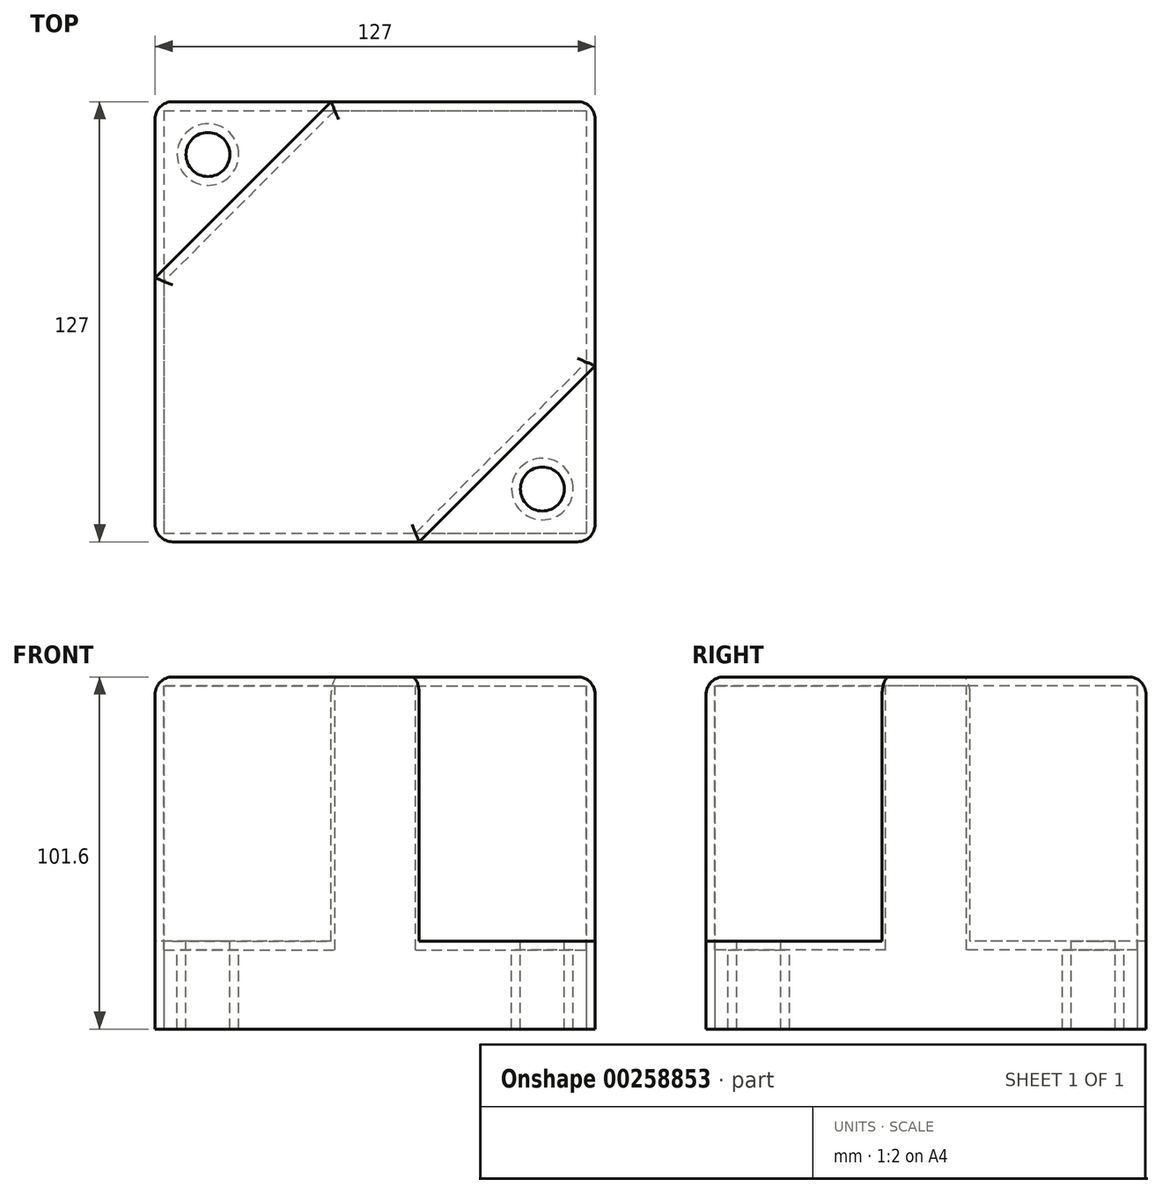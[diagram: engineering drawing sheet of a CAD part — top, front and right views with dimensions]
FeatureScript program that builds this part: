
annotation { "Feature Type Name" : "Feature", "Feature Type Description" : "" }
export const myFeature = defineFeature(function(context is Context, id is Id, definition is map)
    precondition{}
    {
        {
            var Q0;
            Q0=qCreatedBy(makeId("Top.planeOp"),FACE);
            var sketch = newSketch(context, id + "F0", { "sketchPlane" : qUnion([Q0])});
            skLineSegment(sketch, "E0.bottom", {"start": v(-61.5, 64.93) * mm, "end": v(65.5, 64.93) * mm});
            skLineSegment(sketch, "E0.top", {"start": v(-61.5, -62.07) * mm, "end": v(65.5, -62.07) * mm});
            skLineSegment(sketch, "E0.left", {"start": v(-61.5, 64.93) * mm, "end": v(-61.5, -62.07) * mm});
            skLineSegment(sketch, "E0.right", {"start": v(65.5, 64.93) * mm, "end": v(65.5, -62.07) * mm});
            skSolve(sketch);
        }
        {
            var Q0;
            Q0 = qSketchRegion(id + "F0", true);
            var Q1;
            Q1 = qSketchRegion(id + "F2", true);
            extrude(context, id + "F1", {"entities" : qUnion([Q0, Q1]), "depth" : 101.6 * mm});
        }
        {
            var Q0;
            Q0=makeQuery(id+"F1.opExtrude","CAP_FACE",FACE,{"disambiguationData":[OSD([sQuery(id+"F0.wireOp",EDGE,"E0.bottom"),sQuery(id+"F0.wireOp",EDGE,"E0.top"),sQuery(id+"F0.wireOp",EDGE,"E0.left"),sQuery(id+"F0.wireOp",EDGE,"E0.right")])],"isStart":false});
            var sketch = newSketch(context, id + "F2", { "sketchPlane" : qUnion([Q0])});
            skLineSegment(sketch, "E1", {"start": v(-10.7, 64.93) * mm, "end": v(-61.5, 14.13) * mm});
            skLineSegment(sketch, "E2", {"start": v(-10.7, 64.93) * mm, "end": v(-61.5, 64.93) * mm});
            skLineSegment(sketch, "E3", {"start": v(-61.5, 64.93) * mm, "end": v(-61.5, 14.13) * mm});
            skLineSegment(sketch, "E4", {"start": v(14.7, -62.07) * mm, "end": v(65.5, -11.27) * mm});
            skLineSegment(sketch, "E5", {"start": v(65.5, -11.27) * mm, "end": v(65.5, -62.07) * mm});
            skLineSegment(sketch, "E6", {"start": v(65.5, -62.07) * mm, "end": v(14.7, -62.07) * mm});
            skSolve(sketch);
        }
        {
            var Q0;
            Q0=makeQuery(id+"F2.imprint","IMPRINT",FACE,{"disambiguationData":[TD([[makeQuery(id+"F2.imprint","IMPRINT",EDGE,{"derivedFrom":sQuery(id+"F2.wireOp",EDGE,"E1")}),-1.0]])]});
            var Q1;
            Q1=makeQuery(id+"F2.imprint","IMPRINT",FACE,{"disambiguationData":[TD([[makeQuery(id+"F2.imprint","IMPRINT",EDGE,{"derivedFrom":sQuery(id+"F2.wireOp",EDGE,"E4")}),-1.0]])]});
            extrude(context, id + "F3", {"entities" : qUnion([Q0, Q1]), "operationType" : NewBodyOperationType.REMOVE, "oppositeDirection" : true, "depth" : 76.2 * mm});
        }
        {
            var Q0;
            Q0=makeQuery(id+"F3.boolean.opBoolean","COPY",FACE,{"derivedFrom":makeQuery(id+"F3.opExtrude","CAP_FACE",FACE,{"disambiguationData":[OSD([sQuery(id+"F2.wireOp",EDGE,"E1"),sQuery(id+"F2.wireOp",EDGE,"E2"),sQuery(id+"F2.wireOp",EDGE,"E3")])],"isStart":false})});
            var sketch = newSketch(context, id + "F4", { "sketchPlane" : qUnion([Q0])});
            skCircle(sketch, "E7", {"center": v(-46.26, 49.69) * mm, "radius": 6.35 * mm});
            skCircle(sketch, "E8", {"center": v(50.26, -46.83) * mm, "radius": 6.35 * mm});
            skSolve(sketch);
        }
        {
            var Q0;
            Q0 = qSketchRegion(id + "F4", true);
            extrude(context, id + "F5", {"entities" : qUnion([Q0]), "operationType" : NewBodyOperationType.REMOVE, "oppositeDirection" : true, "depth" : 203.2 * mm});
        }
        {
            var Q0;
            Q0=makeQuery(id+"F1.opExtrude","CAP_FACE",FACE,{"disambiguationData":[OSD([sQuery(id+"F0.wireOp",EDGE,"E0.bottom"),sQuery(id+"F0.wireOp",EDGE,"E0.top"),sQuery(id+"F0.wireOp",EDGE,"E0.left"),sQuery(id+"F0.wireOp",EDGE,"E0.right")])],"isStart":true});
            shell(context, id + "F6", {"entities" : qUnion([Q0]), "thickness" : 2.54 * mm});
        }
        {
            var Q0;
            Q0=makeQuery(id+"F3.boolean.opBoolean","COPY",EDGE,{"derivedFrom":makeQuery(id+"F3.opExtrude","CAP_EDGE",EDGE,{"disambiguationData":[OSD([sQuery(id+"F2.wireOp",EDGE,"E1")])],"isStart":true})});
            var Q1;
            Q1=makeQuery(id+"F1.opExtrude","CAP_EDGE",EDGE,{"disambiguationData":[OSD([sQuery(id+"F0.wireOp",EDGE,"E0.left")])],"isStart":false});
            var Q2;
            Q2=makeQuery(id+"F1.opExtrude","CAP_EDGE",EDGE,{"disambiguationData":[OSD([sQuery(id+"F0.wireOp",EDGE,"E0.top")])],"isStart":false});
            var Q3;
            Q3=makeQuery(id+"F1.opExtrude","CAP_FACE",FACE,{"disambiguationData":[OSD([sQuery(id+"F0.wireOp",EDGE,"E0.bottom"),sQuery(id+"F0.wireOp",EDGE,"E0.top"),sQuery(id+"F0.wireOp",EDGE,"E0.left"),sQuery(id+"F0.wireOp",EDGE,"E0.right")])],"isStart":false});
            var Q4;
            Q4=makeQuery(id+"F3.boolean.opBoolean","COPY",EDGE,{"derivedFrom":makeQuery(id+"F3.opExtrude","SWEPT_EDGE",EDGE,{"disambiguationData":[OSD([sQuery(id+"F0.wireOp",EDGE,"E0.left"),sQuery(id+"F2.wireOp",EDGE,"E1"),sQuery(id+"F2.wireOp",EDGE,"E3")])]})});
            var Q5;
            Q5=makeQuery(id+"F3.boolean.opBoolean","COPY",EDGE,{"derivedFrom":makeQuery(id+"F3.opExtrude","SWEPT_EDGE",EDGE,{"disambiguationData":[OSD([sQuery(id+"F0.wireOp",EDGE,"E0.bottom"),sQuery(id+"F2.wireOp",EDGE,"E1"),sQuery(id+"F2.wireOp",EDGE,"E2")])]})});
            var Q6;
            Q6=makeQuery(id+"F3.boolean.opBoolean","COPY",EDGE,{"derivedFrom":makeQuery(id+"F3.opExtrude","CAP_EDGE",EDGE,{"disambiguationData":[OSD([sQuery(id+"F2.wireOp",EDGE,"E3")])],"isStart":false})});
            var Q7;
            Q7=makeQuery(id+"F3.boolean.opBoolean","COPY",EDGE,{"derivedFrom":makeQuery(id+"F3.opExtrude","CAP_EDGE",EDGE,{"disambiguationData":[OSD([sQuery(id+"F2.wireOp",EDGE,"E2")])],"isStart":false})});
            var Q8;
            Q8=makeQuery(id+"F1.opExtrude","SWEPT_EDGE",EDGE,{"disambiguationData":[OSD([sQuery(id+"F0.wireOp",EDGE,"E0.bottom"),sQuery(id+"F0.wireOp",EDGE,"E0.left")])]});
            var Q9;
            Q9=makeQuery(id+"F1.opExtrude","SWEPT_EDGE",EDGE,{"disambiguationData":[OSD([sQuery(id+"F0.wireOp",EDGE,"E0.top"),sQuery(id+"F0.wireOp",EDGE,"E0.left")])]});
            var Q10;
            Q10=makeQuery(id+"F3.boolean.opBoolean","COPY",EDGE,{"derivedFrom":makeQuery(id+"F3.opExtrude","SWEPT_EDGE",EDGE,{"disambiguationData":[OSD([sQuery(id+"F0.wireOp",EDGE,"E0.top"),sQuery(id+"F2.wireOp",EDGE,"E4"),sQuery(id+"F2.wireOp",EDGE,"E6")])]})});
            var Q11;
            Q11=makeQuery(id+"F3.boolean.opBoolean","COPY",EDGE,{"derivedFrom":makeQuery(id+"F3.opExtrude","SWEPT_EDGE",EDGE,{"disambiguationData":[OSD([sQuery(id+"F0.wireOp",EDGE,"E0.right"),sQuery(id+"F2.wireOp",EDGE,"E4"),sQuery(id+"F2.wireOp",EDGE,"E5")])]})});
            var Q12;
            Q12=makeQuery(id+"F3.boolean.opBoolean","COPY",EDGE,{"derivedFrom":makeQuery(id+"F3.opExtrude","CAP_EDGE",EDGE,{"disambiguationData":[OSD([sQuery(id+"F2.wireOp",EDGE,"E5")])],"isStart":false})});
            var Q13;
            Q13=makeQuery(id+"F3.boolean.opBoolean","COPY",EDGE,{"derivedFrom":makeQuery(id+"F3.opExtrude","CAP_EDGE",EDGE,{"disambiguationData":[OSD([sQuery(id+"F2.wireOp",EDGE,"E6")])],"isStart":false})});
            var Q14;
            Q14=makeQuery(id+"F1.opExtrude","SWEPT_EDGE",EDGE,{"disambiguationData":[OSD([sQuery(id+"F0.wireOp",EDGE,"E0.top"),sQuery(id+"F0.wireOp",EDGE,"E0.right")])]});
            var Q15;
            Q15=makeQuery(id+"F1.opExtrude","SWEPT_EDGE",EDGE,{"disambiguationData":[OSD([sQuery(id+"F0.wireOp",EDGE,"E0.bottom"),sQuery(id+"F0.wireOp",EDGE,"E0.right")])]});
            fillet(context, id + "F7", {"entities" : qUnion([Q0, Q1, Q2, Q3, Q4, Q5, Q6, Q7, Q8, Q9, Q10, Q11, Q12, Q13, Q14, Q15]), "radius" : 5.08 * mm, "tangentPropagation" : true, "allowEdgeOverflow" : false});
        }
    });
